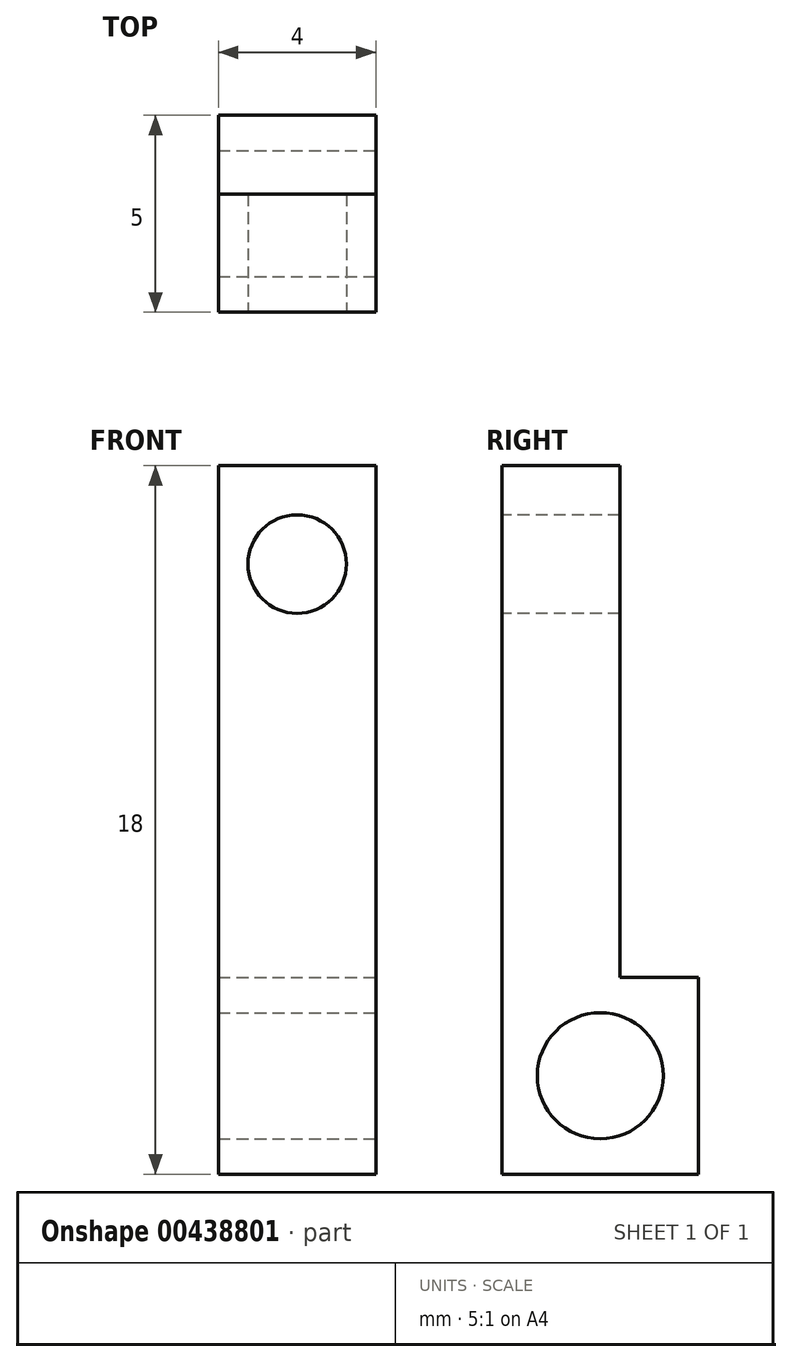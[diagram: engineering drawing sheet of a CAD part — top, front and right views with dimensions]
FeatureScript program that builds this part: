
annotation { "Feature Type Name" : "Feature", "Feature Type Description" : "" }
export const myFeature = defineFeature(function(context is Context, id is Id, definition is map)
    precondition{}
    {
        {
            var Q0;
            Q0=qCreatedBy(makeId("Right.planeOp"),FACE);
            var sketch = newSketch(context, id + "F0", { "sketchPlane" : qUnion([Q0])});
            skCircle(sketch, "E0", {"center": v(0, 0) * mm, "radius": 1.6 * mm});
            skLineSegment(sketch, "E1.bottom", {"start": v(2.5, -2.5) * mm, "end": v(-2.5, -2.5) * mm});
            skLineSegment(sketch, "E1.top", {"start": v(2.5, 2.5) * mm, "end": v(-2.5, 2.5) * mm});
            skLineSegment(sketch, "E1.left", {"start": v(2.5, -2.5) * mm, "end": v(2.5, 2.5) * mm});
            skLineSegment(sketch, "E1.right", {"start": v(-2.5, -2.5) * mm, "end": v(-2.5, 2.5) * mm});
            skLineSegment(sketch, "E2", {"start": v(0.5, 15.5) * mm, "end": v(0.5, 2.5) * mm});
            skLineSegment(sketch, "E3", {"start": v(0.5, 15.5) * mm, "end": v(-2.5, 15.5) * mm});
            skLineSegment(sketch, "E4", {"start": v(-2.5, 2.5) * mm, "end": v(-2.5, 15.5) * mm});
            skLineSegment(sketch, "E5", {"start": v(0.5, 2.5) * mm, "end": v(-2.5, 2.5) * mm});
            skSolve(sketch);
        }
        {
            var Q0;
            Q0 = qSketchRegion(id + "F0", true);
            var Q1;
            Q1=makeQuery(id+"F0.imprint","IMPRINT",FACE,{"disambiguationData":[TD([[makeQuery(id+"F0.imprint","IMPRINT",EDGE,{"derivedFrom":sQuery(id+"F0.wireOp",EDGE,"DIWqbsiE-1YXz-yqfF-bHVn-n5wmmLlW51TL")}),1.0]])]});
            extrude(context, id + "F1", {"entities" : qUnion([Q0, Q1]), "oppositeDirection" : true, "depth" : 4 * mm});
        }
        {
            var Q0;
            Q0=makeQuery(id+"F1.opExtrude","SWEPT_FACE",FACE,{"disambiguationData":[OSD([sQuery(id+"F0.wireOp",EDGE,"E4")])]});
            var sketch = newSketch(context, id + "F2", { "sketchPlane" : qUnion([Q0])});
            skCircle(sketch, "E6", {"center": v(-2, 13) * mm, "radius": 1.25 * mm});
            skPoint(sketch, "E6.centerSnap0", {"position": v(-2, 15.5) * mm});
            skSolve(sketch);
        }
        {
            var Q0;
            Q0=makeQuery(id+"F2.imprint","IMPRINT",FACE,{"disambiguationData":[TD([[makeQuery(id+"F2.imprint","IMPRINT",EDGE,{"derivedFrom":sQuery(id+"F2.wireOp",EDGE,"E6")}),1.0]])]});
            extrude(context, id + "F3", {"entities" : qUnion([Q0]), "operationType" : NewBodyOperationType.REMOVE, "oppositeDirection" : true, "depth" : 25 * mm});
        }
    });
